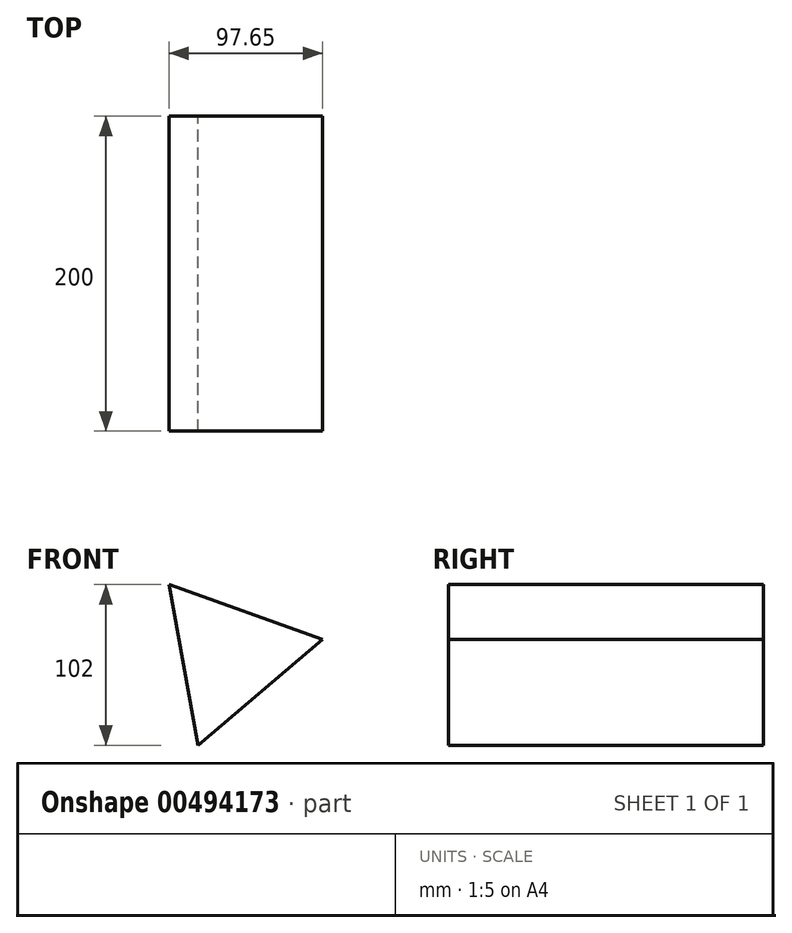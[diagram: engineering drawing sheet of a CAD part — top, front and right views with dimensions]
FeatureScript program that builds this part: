
annotation { "Feature Type Name" : "Feature", "Feature Type Description" : "" }
export const myFeature = defineFeature(function(context is Context, id is Id, definition is map)
    precondition{}
    {
        {
            var Q0;
            Q0=qCreatedBy(makeId("Front.planeOp"),FACE);
            var sketch = newSketch(context, id + "F0", { "sketchPlane" : qUnion([Q0])});
            skCircle(sketch, "E0.cCircle", {"center": v(-3.5, 0) * mm, "radius": 59.86 * mm, "construction": true});
            skLineSegment(sketch, "E0.0", {"start": v(-42.26, 45.62) * mm, "end": v(55.39, 10.76) * mm});
            skLineSegment(sketch, "E0.1", {"start": v(55.39, 10.76) * mm, "end": v(-23.62, -56.38) * mm});
            skLineSegment(sketch, "E0.2", {"start": v(-23.62, -56.38) * mm, "end": v(-42.26, 45.62) * mm});
            skSolve(sketch);
        }
        {
            var Q0;
            Q0=makeQuery(id+"F0.imprint","IMPRINT",FACE,{"disambiguationData":[TD([[makeQuery(id+"F0.imprint","IMPRINT",EDGE,{"derivedFrom":sQuery(id+"F0.wireOp",EDGE,"E0.0")}),-1.0]])]});
            extrude(context, id + "F1", {"entities" : qUnion([Q0]), "endBound" : BoundingType.SYMMETRIC, "depth" : 200 * mm});
        }
    });
